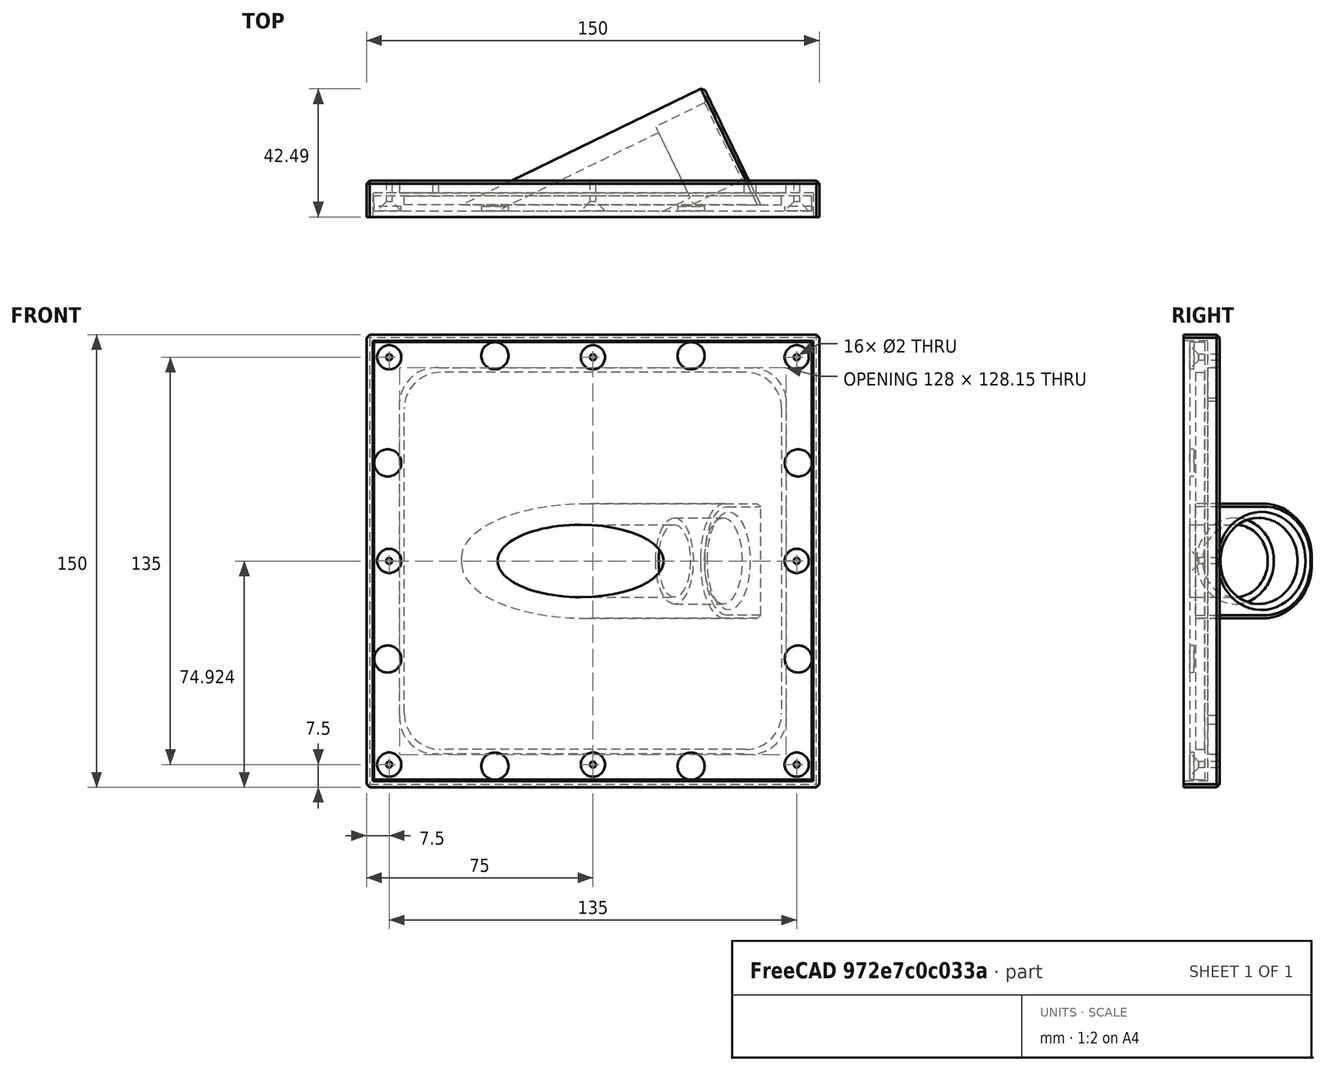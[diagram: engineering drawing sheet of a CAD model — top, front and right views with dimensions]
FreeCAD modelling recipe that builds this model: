
FCSTD DOCUMENT  (FreeCAD 0.18R16110 (Git))
Label: Support_solar_V2
License: All rights reserved
LicenseURL: http://en.wikipedia.org/wiki/All_rights_reserved
objects: Sketcher::SketchObject×11, PartDesign::Pocket×6, PartDesign::Pad×5, PartDesign::Chamfer×4, PartDesign::Body×2, Mesh::Feature×2, PartDesign::Fillet×1
note: 40 computed .brp shape members not serialized (recipe doc carries the construction recipe); baked Part::Feature solids carry a one-line shape summary decoded from their .brp

FEATURE [Sketcher::SketchObject] Sketch
  MapMode = 5
  Support = -> [XY_Plane]
  sketch-geometry (3):
    g0: LineSegment StartX=19 StartY=-50 StartZ=0 EndX=19 EndY=39.129 EndZ=0
    g1: LineSegment StartX=19 StartY=39.129 StartZ=0 EndX=-24.2787 EndY=-50 EndZ=0
    g2: LineSegment StartX=-24.2787 StartY=-50 StartZ=0 EndX=19 EndY=-50 EndZ=0
  constraints (9):
    c: Horizontal(g2)
    c: Coincident(g0,g1)
    c: DistanceX(g-2,g0) = 19
    c: Vertical(g0)
    c: Angle(g1,g0) = 0.45204
    c: Coincident(g1,g2)
    c: Coincident(g2,g0)
    c: PointOnObject(g-1,g1)
    c: Distance(g-1,g2) = 50
FEATURE [PartDesign::Pad] Pad
  Length = 38
  Length2 = 100
  Midplane = true
  Profile = -> Sketch
  Type = 0
FEATURE [Sketcher::SketchObject] Sketch001
  MapMode = 5
  Placement = pos=(0,-50,0) rot=(1,0,0;1.5708rad)
  Support = -> [Pad]
  sketch-geometry (1):
    g0: Circle CenterX=0 CenterY=0 CenterZ=0 NormalX=0 NormalY=0 NormalZ=1 AngleXU=0 Radius=12
  constraints (2):
    c: Coincident(g0,g-1)
    c: Radius(g0) = 12
FEATURE [PartDesign::Pocket] Pocket
  BaseFeature = -> Pad
  Length = 100
  Length2 = 100
  Profile = -> Sketch001
  Type = 0
FEATURE [PartDesign::Fillet] Fillet
  Base = -> Pocket [Edge4,Edge3]
  BaseFeature = -> Pocket
  Radius = 18
FEATURE [Sketcher::SketchObject] Sketch002
  ExternalGeometry = -> [Fillet]
  MapMode = 5
  Placement = pos=(0,-50,0) rot=(1,0,0;1.5708rad)
  Support = -> [Fillet]
  sketch-geometry (1):
    g0: Circle CenterX=0 CenterY=0 CenterZ=0 NormalX=0 NormalY=0 NormalZ=1 AngleXU=0 Radius=14.25
  constraints (2):
    c: Coincident(g0,g-1)
    c: Radius(g0) = 14.25
FEATURE [PartDesign::Pocket] Pocket001
  BaseFeature = -> Fillet
  Length = 20
  Length2 = 100
  Profile = -> Sketch002
  Type = 0
FEATURE [Sketcher::SketchObject] Sketch003
  MapMode = 5
  Placement = pos=(-3.2e-15,1.6e-15,0) rot=(-0.404812,0.646578,0.646578;3.91089rad)
  Support = -> [Pocket001]
  sketch-geometry (4):
    g0: LineSegment StartX=-72.5 StartY=72.5 StartZ=0 EndX=72.5 EndY=72.5 EndZ=0
    g1: LineSegment StartX=72.5 StartY=72.5 StartZ=0 EndX=72.5 EndY=-72.5 EndZ=0
    g2: LineSegment StartX=72.5 StartY=-72.5 StartZ=0 EndX=-72.5 EndY=-72.5 EndZ=0
    g3: LineSegment StartX=-72.5 StartY=-72.5 StartZ=0 EndX=-72.5 EndY=72.5 EndZ=0
  constraints (10):
    c: Coincident(g0,g1)
    c: Coincident(g1,g2)
    c: Coincident(g2,g3)
    c: Coincident(g3,g0)
    c: Horizontal(g2)
    c: Vertical(g1)
    c: Symmetric(g0,g0,g-2)
    c: Symmetric(g0,g2,g-1)
    c: Equal(g3,g0)
    c: DistanceY(g3,g3) = 145
FEATURE [PartDesign::Pad] Pad001
  BaseFeature = -> Pocket001
  Length = 2
  Length2 = 100
  Profile = -> Sketch003
  Type = 0
FEATURE [Sketcher::SketchObject] Sketch004
  ExternalGeometry = -> [Pad001]
  MapMode = 5
  Placement = pos=(0,-30,0) rot=(1,0,0;1.5708rad)
  Support = -> [Pad001]
  sketch-geometry (1):
    g0: Circle CenterX=0 CenterY=0 CenterZ=0 NormalX=0 NormalY=0 NormalZ=1 AngleXU=0 Radius=12
  constraints (2):
    c: Coincident(g0,g-1)
    c: Tangent(g0,g-3)
FEATURE [PartDesign::Pocket] Pocket002
  BaseFeature = -> Pad001
  Length = 100
  Length2 = 100
  Profile = -> Sketch004
  Type = 0
FEATURE [Sketcher::SketchObject] Sketch005
  ExternalGeometry = -> [Pocket002]
  MapMode = 5
  Placement = pos=(-1.79912,0.873604,0) rot=(-0.404812,0.646578,0.646578;3.91089rad)
  Support = -> [Pocket002]
  sketch-geometry (4):
    g0: Circle CenterX=-32.5 CenterY=68 CenterZ=0 NormalX=0 NormalY=0 NormalZ=1 AngleXU=0 Radius=4.5
    g1: Circle CenterX=32.5 CenterY=68 CenterZ=0 NormalX=0 NormalY=0 NormalZ=1 AngleXU=0 Radius=4.5
    g2: Circle CenterX=-32.5 CenterY=-68 CenterZ=0 NormalX=0 NormalY=0 NormalZ=1 AngleXU=0 Radius=4.5
    g3: Circle CenterX=32.5 CenterY=-68 CenterZ=0 NormalX=0 NormalY=0 NormalZ=1 AngleXU=0 Radius=4.5
  constraints (9):
    c: Radius(g3) = 4.5
    c: Equal(g3,g2)
    c: Equal(g3,g0)
    c: Equal(g3,g1)
    c: Distance(g0,g-3) = 40
    c: Distance(g0,g-4) = 4.5
    c: Symmetric(g0,g1,g-2)
    c: Symmetric(g0,g2,g-1)
    c: Symmetric(g1,g3,g-1)
FEATURE [PartDesign::Pocket] Pocket003
  BaseFeature = -> Pocket002
  Length = 1.5
  Length2 = 100
  Profile = -> Sketch005
  Type = 0
FEATURE [Sketcher::SketchObject] Sketch006
  ExternalGeometry = -> [Pocket003]
  MapMode = 5
  Placement = pos=(-5.1e-15,2.5e-15,0) rot=(0.748699,0.468748,0.468748;1.85626rad)
  Support = -> [Pocket003]
  sketch-geometry (12):
    g0: ArcOfCircle CenterX=-50.5 CenterY=50.5 CenterZ=0 NormalX=0 NormalY=0 NormalZ=1 AngleXU=0 Radius=12 StartAngle=1.5708 EndAngle=3.14159
    g1: ArcOfCircle CenterX=50.5 CenterY=50.5 CenterZ=0 NormalX=0 NormalY=0 NormalZ=1 AngleXU=0 Radius=12 StartAngle=9.65186e-10 EndAngle=1.5708
    g2: ArcOfCircle CenterX=-50.5 CenterY=-50.5 CenterZ=0 NormalX=0 NormalY=0 NormalZ=1 AngleXU=0 Radius=12 StartAngle=3.14159 EndAngle=4.71239
    g3: ArcOfCircle CenterX=50.5 CenterY=-50.5 CenterZ=0 NormalX=0 NormalY=0 NormalZ=1 AngleXU=0 Radius=12 StartAngle=4.71239 EndAngle=6.28319
    g4: LineSegment StartX=-50.5 StartY=62.5 StartZ=0 EndX=50.5 EndY=62.5 EndZ=0
    g5: LineSegment StartX=-50.5 StartY=-62.5 StartZ=0 EndX=50.5 EndY=-62.5 EndZ=0
    g6: LineSegment StartX=62.5 StartY=-50.5 StartZ=0 EndX=62.5 EndY=50.5 EndZ=0
    g7: LineSegment StartX=-62.5 StartY=50.5 StartZ=0 EndX=-62.5 EndY=-50.5 EndZ=0
    g8: LineSegment StartX=-72.5 StartY=72.5 StartZ=0 EndX=72.5 EndY=72.5 EndZ=0
    g9: LineSegment StartX=72.5 StartY=72.5 StartZ=0 EndX=72.5 EndY=-72.5 EndZ=0
    g10: LineSegment StartX=72.5 StartY=-72.5 StartZ=0 EndX=-72.5 EndY=-72.5 EndZ=0
    g11: LineSegment StartX=-72.5 StartY=-72.5 StartZ=0 EndX=-72.5 EndY=72.5 EndZ=0
  constraints (30):
    c: Coincident(g4,g0)
    c: Coincident(g4,g1)
    c: Coincident(g5,g2)
    c: Horizontal(g5)
    c: Coincident(g6,g3)
    c: Coincident(g6,g1)
    c: Vertical(g6)
    c: Coincident(g7,g0)
    c: Coincident(g7,g2)
    c: Coincident(g3,g5)
    c: Radius(g0) = 12
    c: Distance(g0,g-5) = 10
    c: Distance(g0,g-3) = 10
    c: Symmetric(g0,g1,g-2)
    c: Symmetric(g2,g0,g-1)
    c: Symmetric(g0,g1,g-2)
    c: Symmetric(g0,g2,g-1)
    c: Angle(g0) = 1.5708
    c: Symmetric(g2,g3,g-2)
    c: Symmetric(g0,g1,g-2)
    c: Coincident(g8,g9)
    c: Coincident(g9,g10)
    c: Coincident(g10,g11)
    c: Coincident(g11,g8)
    c: Horizontal(g8)
    c: Horizontal(g10)
    c: Vertical(g9)
    c: Vertical(g11)
    c: Coincident(g8,g-5)
    c: Coincident(g9,g-6)
FEATURE [PartDesign::Pad] Pad002
  BaseFeature = -> Pocket003
  Length = 3
  Length2 = 100
  Profile = -> Sketch006
  Type = 0
FEATURE [Sketcher::SketchObject] Sketch007
  ExternalGeometry = -> [Pad002]
  MapMode = 5
  Placement = pos=(-1.79912,0.873604,0) rot=(-0.404812,0.646578,0.646578;3.91089rad)
  Support = -> [Pad002]
  sketch-geometry (8):
    g0: Circle CenterX=-67.5 CenterY=67.5 CenterZ=0 NormalX=0 NormalY=0 NormalZ=1 AngleXU=0 Radius=1
    g1: Circle CenterX=67.5 CenterY=67.5 CenterZ=0 NormalX=0 NormalY=0 NormalZ=1 AngleXU=0 Radius=1
    g2: Circle CenterX=0 CenterY=67.5 CenterZ=0 NormalX=0 NormalY=0 NormalZ=1 AngleXU=0 Radius=1
    g3: Circle CenterX=0 CenterY=-67.5 CenterZ=0 NormalX=0 NormalY=0 NormalZ=1 AngleXU=0 Radius=1
    g4: Circle CenterX=67.5 CenterY=-67.5 CenterZ=0 NormalX=0 NormalY=0 NormalZ=1 AngleXU=0 Radius=1
    g5: Circle CenterX=-67.5 CenterY=-67.5 CenterZ=0 NormalX=0 NormalY=0 NormalZ=1 AngleXU=0 Radius=1
    g6: Circle CenterX=-67.5 CenterY=0 CenterZ=0 NormalX=0 NormalY=0 NormalZ=1 AngleXU=0 Radius=1
    g7: Circle CenterX=67.5 CenterY=0 CenterZ=0 NormalX=0 NormalY=0 NormalZ=1 AngleXU=0 Radius=1
  constraints (19):
    c: PointOnObject(g2,g-2)
    c: PointOnObject(g7,g-1)
    c: Radius(g0) = 1
    c: Equal(g0,g2)
    c: Equal(g0,g1)
    c: Equal(g0,g7)
    c: Equal(g0,g4)
    c: Equal(g0,g3)
    c: Equal(g0,g5)
    c: Equal(g0,g6)
    c: Symmetric(g6,g7,g-2)
    c: Symmetric(g0,g1,g-2)
    c: Symmetric(g5,g4,g-2)
    c: Symmetric(g5,g0,g-1)
    c: Symmetric(g2,g3,g-1)
    c: Distance(g2,g-4) = 5
    c: Distance(g1,g-5) = 5
    c: Distance(g1,g-6) = 5
    c: Distance(g6,g-7) = 5
FEATURE [PartDesign::Pocket] Pocket004
  BaseFeature = -> Pad002
  Length = 8
  Length2 = 100
  Profile = -> Sketch007
  Type = 0
FEATURE [PartDesign::Chamfer] Chamfer
  Base = -> Pocket004 [Edge34,Edge33,Edge35,Edge20,Edge25,Edge30,Edge26,Edge27]
  BaseFeature = -> Pocket004
  Size = 3
FEATURE [PartDesign::Chamfer] Chamfer001
  Base = -> Chamfer [Edge120]
  BaseFeature = -> Chamfer
  Size = 2
FEATURE [PartDesign::Chamfer] Chamfer002
  Base = -> Chamfer001 [Edge7]
  BaseFeature = -> Chamfer001
  Size = 1
FEATURE [Sketcher::SketchObject] Sketch008
  ExternalGeometry = -> [Chamfer002]
  MapMode = 5
  Placement = pos=(-1.79912,0.873604,0) rot=(-0.404812,0.646578,0.646578;3.91089rad)
  Support = -> [Chamfer002]
  sketch-geometry (4):
    g0: Circle CenterX=-68 CenterY=32.5 CenterZ=0 NormalX=0 NormalY=0 NormalZ=1 AngleXU=0 Radius=4.5
    g1: Circle CenterX=-68 CenterY=-32.5 CenterZ=0 NormalX=0 NormalY=0 NormalZ=1 AngleXU=0 Radius=4.5
    g2: Circle CenterX=68 CenterY=32.5 CenterZ=0 NormalX=0 NormalY=0 NormalZ=1 AngleXU=0 Radius=4.5
    g3: Circle CenterX=68 CenterY=-32.5 CenterZ=0 NormalX=0 NormalY=0 NormalZ=1 AngleXU=0 Radius=4.5
  constraints (9):
    c: Radius(g2) = 4.5
    c: Equal(g2,g3)
    c: Equal(g2,g1)
    c: Equal(g2,g0)
    c: Symmetric(g0,g1,g-1)
    c: Symmetric(g2,g3,g-1)
    c: Symmetric(g0,g2,g-2)
    c: Distance(g0,g-3) = 40
    c: Distance(g0,g-4) = 4.5
FEATURE [PartDesign::Pocket] Pocket005
  BaseFeature = -> Chamfer002
  Length = 1.5
  Length2 = 100
  Profile = -> Sketch008
  Type = 0
FEATURE [PartDesign::Body] Body
  Group = -> [Sketch,Pad,Sketch001,Pocket,Fillet,Sketch002,Pocket001,Sketch003,Pad001,Sketch004,Pocket002,Sketch005,Pocket003,Sketch006,Pad002,Sketch007,Pocket004,Chamfer,Chamfer001,Chamfer002,Sketch008,Pocket005]
  Origin = -> Origin
  Placement = pos=(0,0,0) rot=(0,0,1;2.02284rad)
  Tip = -> Pocket005
FEATURE [Mesh::Feature] Mesh  label="Body (Meshed)"
FEATURE [Sketcher::SketchObject] Sketch009
  MapMode = 5
  Placement = pos=(0,0,0) rot=(1,0,0;1.5708rad)
  Support = -> [XZ_Plane001]
  sketch-geometry (8):
    g0: LineSegment StartX=-73 StartY=73 StartZ=0 EndX=73 EndY=73 EndZ=0
    g1: LineSegment StartX=73 StartY=73 StartZ=0 EndX=73 EndY=-73 EndZ=0
    g2: LineSegment StartX=73 StartY=-73 StartZ=0 EndX=-73 EndY=-73 EndZ=0
    g3: LineSegment StartX=-73 StartY=-73 StartZ=0 EndX=-73 EndY=73 EndZ=0
    g4: LineSegment StartX=-75 StartY=75 StartZ=0 EndX=75 EndY=75 EndZ=0
    g5: LineSegment StartX=75 StartY=75 StartZ=0 EndX=75 EndY=-75 EndZ=0
    g6: LineSegment StartX=75 StartY=-75 StartZ=0 EndX=-75 EndY=-75 EndZ=0
    g7: LineSegment StartX=-75 StartY=-75 StartZ=0 EndX=-75 EndY=75 EndZ=0
  constraints (20):
    c: Coincident(g0,g1)
    c: Coincident(g1,g2)
    c: Coincident(g2,g3)
    c: Coincident(g3,g0)
    c: Horizontal(g2)
    c: Vertical(g1)
    c: Symmetric(g0,g2,g-1)
    c: Symmetric(g0,g0,g-2)
    c: Equal(g0,g3)
    c: DistanceY(g3,g3) = 146
    c: Coincident(g4,g5)
    c: Coincident(g5,g6)
    c: Coincident(g6,g7)
    c: Coincident(g7,g4)
    c: Horizontal(g6)
    c: Vertical(g7)
    c: Distance(g4,g3) = 2
    c: Distance(g4,g0) = 2
    c: Symmetric(g4,g4,g-2)
    c: Symmetric(g4,g5,g-1)
FEATURE [PartDesign::Pad] Pad003
  Length = 8
  Length2 = 100
  Placement = pos=(0,0,0) rot=(1,0,0;1.5708rad)
  Profile = -> Sketch009
  Type = 0
FEATURE [Sketcher::SketchObject] Sketch010
  ExternalGeometry = -> [Pad003]
  MapMode = 5
  Placement = pos=(0,0,0) rot=(-1,0,0;1.5708rad)
  Support = -> [Pad003]
  sketch-geometry (20):
    g0: LineSegment StartX=-75 StartY=75 StartZ=0 EndX=75 EndY=75 EndZ=0
    g1: LineSegment StartX=75 StartY=75 StartZ=0 EndX=75 EndY=-75 EndZ=0
    g2: LineSegment StartX=75 StartY=-75 StartZ=0 EndX=-75 EndY=-75 EndZ=0
    g3: LineSegment StartX=-75 StartY=-75 StartZ=0 EndX=-75 EndY=75 EndZ=0
    g4: ArcOfCircle CenterX=-52.0386 CenterY=52.0386 CenterZ=0 NormalX=0 NormalY=0 NormalZ=1 AngleXU=0 Radius=12 StartAngle=1.651 EndAngle=3.2218
    g5: ArcOfCircle CenterX=52.0386 CenterY=52.0386 CenterZ=0 NormalX=0 NormalY=0 NormalZ=1 AngleXU=0 Radius=12.1212 StartAngle=0.162533 EndAngle=1.73333
    g6: ArcOfCircle CenterX=52.0386 CenterY=-52.0386 CenterZ=0 NormalX=0 NormalY=0 NormalZ=1 AngleXU=0 Radius=12.1212 StartAngle=4.87492 EndAngle=6.12065
    g7: ArcOfCircle CenterX=-52.0386 CenterY=-52.0386 CenterZ=0 NormalX=0 NormalY=0 NormalZ=1 AngleXU=0 Radius=12 StartAngle=3.2218 EndAngle=4.79259
    g8: LineSegment StartX=-64 StartY=51.0772 StartZ=0 EndX=-64 EndY=-53 EndZ=0
    g9: LineSegment StartX=-51.0772 StartY=-64 StartZ=0 EndX=54 EndY=-64 EndZ=0
    g10: LineSegment StartX=64 StartY=-54 StartZ=0 EndX=64 EndY=54 EndZ=0
    g11: LineSegment StartX=50.0772 StartY=64 StartZ=0 EndX=-53 EndY=64 EndZ=0
    g12: Circle CenterX=-67.5 CenterY=67.5 CenterZ=0 NormalX=0 NormalY=0 NormalZ=1 AngleXU=0 Radius=1
    g13: Circle CenterX=67.5 CenterY=67.5 CenterZ=0 NormalX=0 NormalY=0 NormalZ=1 AngleXU=0 Radius=1
    g14: Circle CenterX=0 CenterY=67.5 CenterZ=0 NormalX=0 NormalY=0 NormalZ=1 AngleXU=0 Radius=1
    g15: Circle CenterX=-67.5 CenterY=0 CenterZ=0 NormalX=0 NormalY=0 NormalZ=1 AngleXU=0 Radius=1
    g16: Circle CenterX=-67.5 CenterY=-67.5 CenterZ=0 NormalX=0 NormalY=0 NormalZ=1 AngleXU=0 Radius=1
    g17: Circle CenterX=0 CenterY=-67.5 CenterZ=0 NormalX=0 NormalY=0 NormalZ=1 AngleXU=0 Radius=1
    g18: Circle CenterX=67.5 CenterY=-67.5 CenterZ=0 NormalX=0 NormalY=0 NormalZ=1 AngleXU=0 Radius=1
    g19: Circle CenterX=67.5 CenterY=0 CenterZ=0 NormalX=0 NormalY=0 NormalZ=1 AngleXU=0 Radius=1
  constraints (53):
    c: Coincident(g0,g1)
    c: Coincident(g1,g2)
    c: Coincident(g2,g3)
    c: Coincident(g3,g0)
    c: Horizontal(g0)
    c: Horizontal(g2)
    c: Vertical(g1)
    c: Vertical(g3)
    c: Coincident(g0,g-4)
    c: Coincident(g1,g-6)
    c: Coincident(g8,g4)
    c: Coincident(g8,g7)
    c: Vertical(g8)
    c: Coincident(g9,g7)
    c: Coincident(g9,g6)
    c: Horizontal(g9)
    c: Coincident(g10,g6)
    c: Coincident(g10,g5)
    c: Vertical(g10)
    c: Coincident(g11,g5)
    c: Coincident(g11,g4)
    c: Radius(g4) = 12
    c: Angle(g7) = 1.5708
    c: Angle(g4) = 1.5708
    c: Angle(g5) = 1.5708
    c: Symmetric(g7,g6,g-2)
    c: Symmetric(g7,g4,g-1)
    c: Symmetric(g5,g6,g-1)
    c: Distance(g4,g3) = 11
    c: Distance(g4,g0) = 11
    c: Horizontal(g11)
    c: Distance(g5,g0) = 21
    c: Distance(g6,g2) = 21
    c: PointOnObject(g17,g-2)
    c: PointOnObject(g19,g-1)
    c: Radius(g19) = 1
    c: Equal(g19,g13)
    c: Equal(g19,g14)
    c: Equal(g19,g12)
    c: Equal(g19, g15-g18) x4
    c: Distance(g19,g1) = 7.5
    c: Distance(g18,g1) = 7.5
    c: Distance(g18,g2) = 7.5
    c: Distance(g17,g2) = 7.5
    c: Distance(g16,g2) = 7.5
    c: Distance(g16,g3) = 7.5
    c: PointOnObject(g15,g-1)
    c: Distance(g15,g3) = 7.5
    c: Symmetric(g16,g12,g-1)
    c: Symmetric(g17,g14,g-1)
    c: Symmetric(g13,g18,g-1)
    c: Distance(g4,g3) = 22
    c: Distance(g7,g2) = 22
FEATURE [PartDesign::Pad] Pad004
  BaseFeature = -> Pad003
  Length = 4
  Length2 = 100
  Placement = pos=(0,0,0) rot=(1,0,0;1.5708rad)
  Profile = -> Sketch010
  Type = 0
FEATURE [PartDesign::Chamfer] Chamfer003
  Base = -> Pad004 [Edge24,Edge21,Edge13,Edge23,Edge22,Edge2,Edge5,Edge1]
  BaseFeature = -> Pad004
  Placement = pos=(0,0,0) rot=(1,0,0;1.5708rad)
  Size = 1
FEATURE [PartDesign::Body] Body001  label="Contour"
  Group = -> [Sketch009,Pad003,Sketch010,Pad004,Chamfer003]
  Origin = -> Origin001
  Placement = pos=(0,4,0) rot=(0,0,1;0rad)
  Tip = -> Chamfer003
FEATURE [Mesh::Feature] Mesh001  label="Contour (Meshed)"
